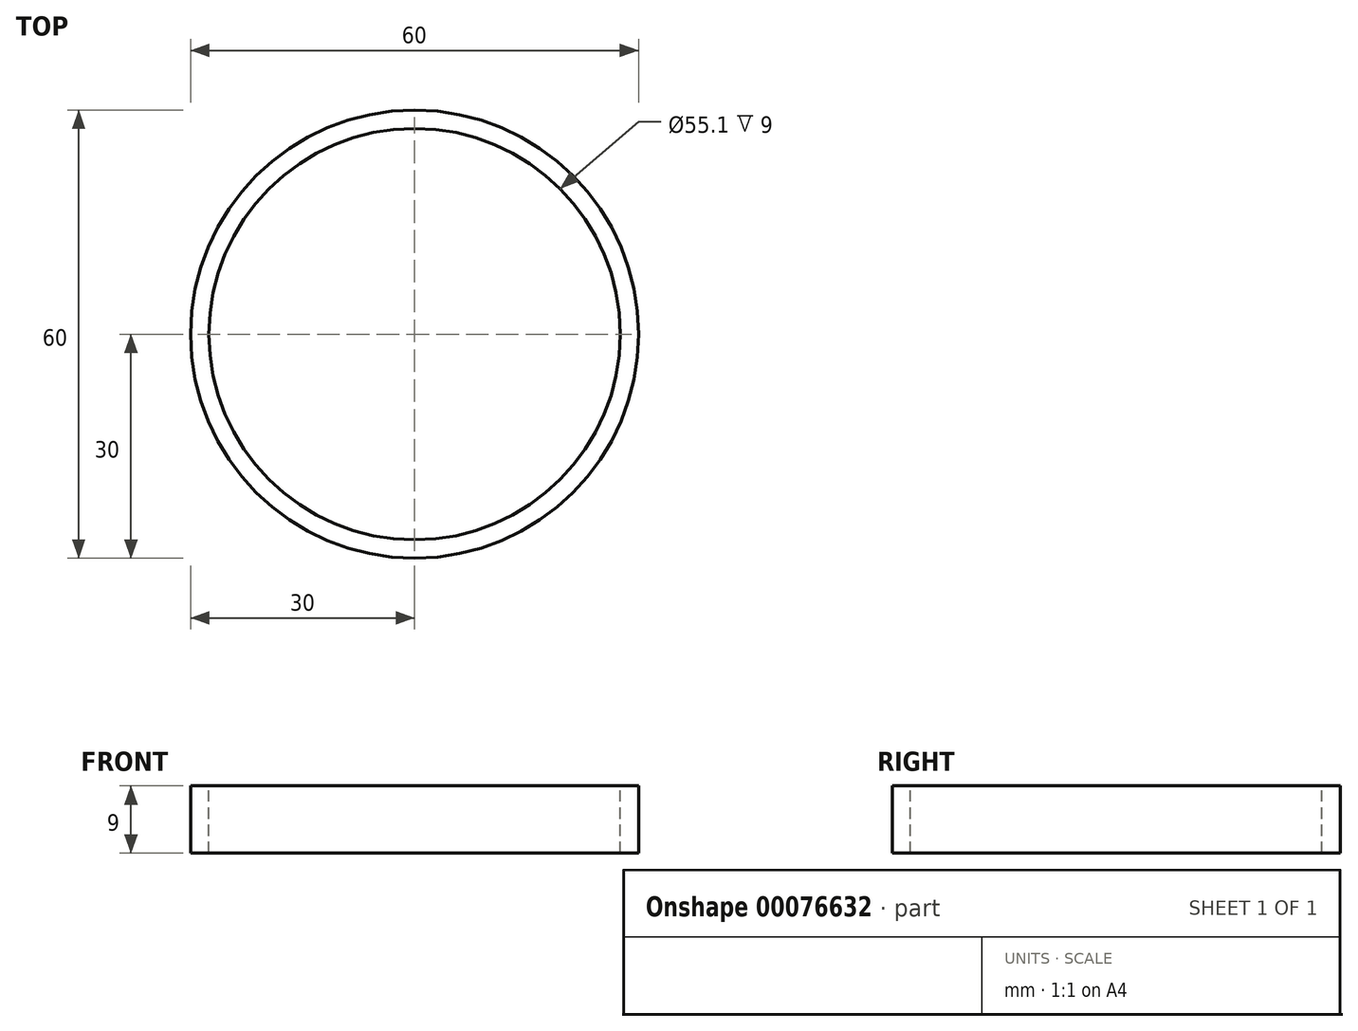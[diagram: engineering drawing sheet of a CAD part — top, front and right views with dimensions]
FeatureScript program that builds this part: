
annotation { "Feature Type Name" : "Feature", "Feature Type Description" : "" }
export const myFeature = defineFeature(function(context is Context, id is Id, definition is map)
    precondition{}
    {
        {
            var Q0;
            Q0=qCreatedBy(makeId("Top.planeOp"),FACE);
            var sketch = newSketch(context, id + "F0", { "sketchPlane" : qUnion([Q0])});
            skCircle(sketch, "E0", {"center": v(0, 0) * mm, "radius": 30 * mm});
            skSolve(sketch);
        }
        {
            var Q0;
            Q0 = qSketchRegion(id + "F0", true);
            extrude(context, id + "F1", {"entities" : qUnion([Q0]), "depth" : 9 * mm});
        }
        {
            var Q0;
            Q0=makeQuery(id+"F1.opExtrude","CAP_FACE",FACE,{"disambiguationData":[OSD([sQuery(id+"F0.wireOp",EDGE,"E0")])],"isStart":false});
            var sketch = newSketch(context, id + "F2", { "sketchPlane" : qUnion([Q0])});
            skCircle(sketch, "E1", {"center": v(0, 0) * mm, "radius": 27.55 * mm});
            skSolve(sketch);
        }
        {
            var Q0;
            Q0=makeQuery(id+"F2.imprint","IMPRINT",FACE,{"disambiguationData":[TD([[makeQuery(id+"F2.imprint","IMPRINT",EDGE,{"derivedFrom":sQuery(id+"F2.wireOp",EDGE,"E1")}),1.0]])]});
            var Q1;
            Q1=sQuery(id+"F2.wireOp",EDGE,"E1");
            extrude(context, id + "F3", {"entities" : qUnion([Q0]), "operationType" : NewBodyOperationType.REMOVE, "surfaceEntities" : qUnion([Q1]), "oppositeDirection" : true, "depth" : 9 * mm});
        }
    });
